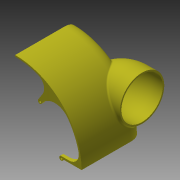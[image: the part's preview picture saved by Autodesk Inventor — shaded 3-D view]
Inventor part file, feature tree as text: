
AUTODESK INVENTOR PART (.ipt)
format: ipt  version: 2015 (Build 190159000, 159)  size: 729,088 bytes
history: native  units: mm
features: sketch x13, extrude x9, revolve x5, fillet x5
ambient origin geometry x8: Origin, YZ Plane, XZ Plane, XY Plane, X Axis, Y Axis, Z Axis, Center Point
bodies: Body1 (feature_tree)
feature tree (32):
  sketch  "Boceto1"  dims[d1=40.0mm d2=20.0mm d3=20.0mm d4=5.0mm d5=360.0deg d6=5.0mm d7=5.0mm d9=5.0mm d10=10.0mm d11=2.451216mm d13=270.0mm]
  revolve  "Revolución1"  [1 undecoded]
  sketch  "Boceto3"  dims[d20=3.0mm d21=120.0mm]
  extrude  "Extrusión2"  Depth=100.0mm
  extrude  "Extrusión3"  Depth=120.0mm
  sketch  "Boceto6"  dims[d22=3.0mm d23=120.0mm]
  revolve  "Revolución2"  [1 undecoded]
  revolve  "Revolución3"  [1 undecoded]
  revolve  "Revolución4"  [1 undecoded]
  revolve  "Revolución5"  [1 undecoded]
  fillet  "Empalme2"  Radius=100.0mm
  sketch  "Boceto7"  dims[d24=90.0deg]
  extrude  "Extrusión7"  Depth=20.0mm
  extrude  "Extrusión8"  Depth=3.0mm
  extrude  "Extrusión9"  TaperAngle=90.0deg  [1 undecoded]
  extrude  "Extrusión10"  TaperAngle=90.0deg  [1 undecoded]
  fillet  "Empalme4"  Radius=3.0mm
  fillet  "Empalme5"  Radius=20.0mm
  sketch  "Boceto16"  dims[d57=135.0mm d58=3.0mm]
  extrude  "Extrusión11"  Depth=10.0mm
  extrude  "Extrusión12"  Depth=10.0mm
  fillet  "Empalme6"  Radius=111.0mm
  extrude  "Extrusión13"  Depth=8.0mm
  fillet  "Empalme7"  Radius=8.0mm
  sketch  "Boceto2"  dims[d14=3.0mm d19=100.0mm]
  sketch  "Boceto11"  dims[d26=40.0mm d27=20.0mm d28=20.0mm d29=5.0mm d30=360.0deg d31=5.0mm d32=5.0mm d33=5.0mm d34=10.0mm d35=2.451216mm d36=270.0mm d37=3.0mm d38=60.0mm d39=0.0mm]
  sketch  "Boceto12"  dims[d40=3.0mm d41=0.0mm d51=20.0mm]
  sketch  "Boceto13"  dims[d52=45.0mm d53=20.0mm d54=100.0mm]
  sketch  "Boceto14"  dims[d55=90.0deg d56=20.0mm]
  sketch  "Boceto17"  dims[d59=90.0deg d60=90.0deg]
  sketch  "Boceto18"  dims[d61=90.0deg d62=90.0deg d63=3.0mm d69=20.0mm]
  sketch  "Boceto19"  dims[d70=10.0mm d71=10.0mm d73=10.0mm d74=111.0mm d75=0.0mm d79=8.0mm d80=8.0mm d81=8.0mm d82=8.0mm d83=6.0mm d84=0.0mm d87=20.0mm d89=360.0deg d91=6.0mm d92=0.0mm d93=6.0mm d94=0.0mm d95=30.0mm d96=20.0mm d97=60.0deg d98=1111.0mm d99=0.0mm d100=6.0mm d101=0.0mm d102=1.0mm d103=6.0mm d104=0.0mm d105=2.0mm]
note: 7 required parameter values undecoded (feature->parameter linkage not recoverable at this tier; creation-order binding heuristic only, values carry confidence <= 0.55)